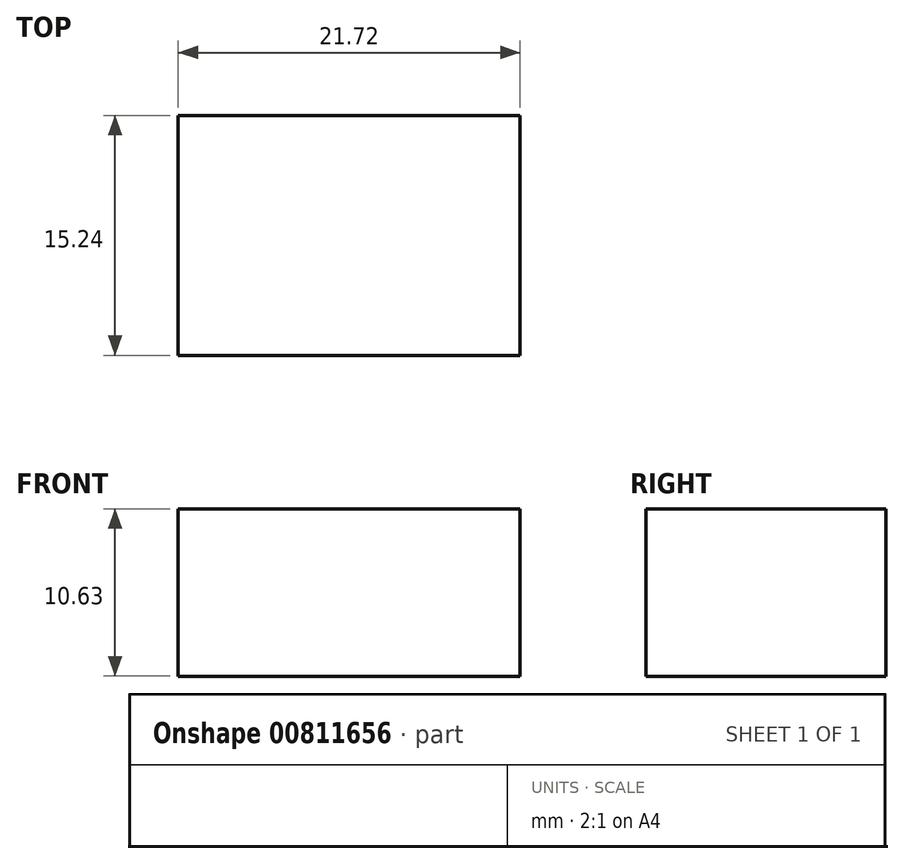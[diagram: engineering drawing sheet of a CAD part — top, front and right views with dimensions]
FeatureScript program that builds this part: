
annotation { "Feature Type Name" : "Feature", "Feature Type Description" : "" }
export const myFeature = defineFeature(function(context is Context, id is Id, definition is map)
    precondition{}
    {
        {
            var Q0;
            Q0=qCreatedBy(makeId("Front.planeOp"),FACE);
            var sketch = newSketch(context, id + "F0", { "sketchPlane" : qUnion([Q0])});
            skLineSegment(sketch, "E0.bottom", {"start": v(41.12, 32.68) * mm, "end": v(19.4, 32.68) * mm});
            skLineSegment(sketch, "E0.top", {"start": v(41.12, 22.05) * mm, "end": v(19.4, 22.05) * mm});
            skLineSegment(sketch, "E0.left", {"start": v(41.12, 32.68) * mm, "end": v(41.12, 22.05) * mm});
            skLineSegment(sketch, "E0.right", {"start": v(19.4, 32.68) * mm, "end": v(19.4, 22.05) * mm});
            skPoint(sketch, "E0.middle", {"position": v(30.26, 27.36) * mm});
            skSolve(sketch);
        }
        {
            var Q0;
            Q0 = qSketchRegion(id + "F0", true);
            extrude(context, id + "F1", {"entities" : qUnion([Q0]), "depth" : 15.24 * mm, "offsetDistance" : 25.4 * mm});
        }
    });
